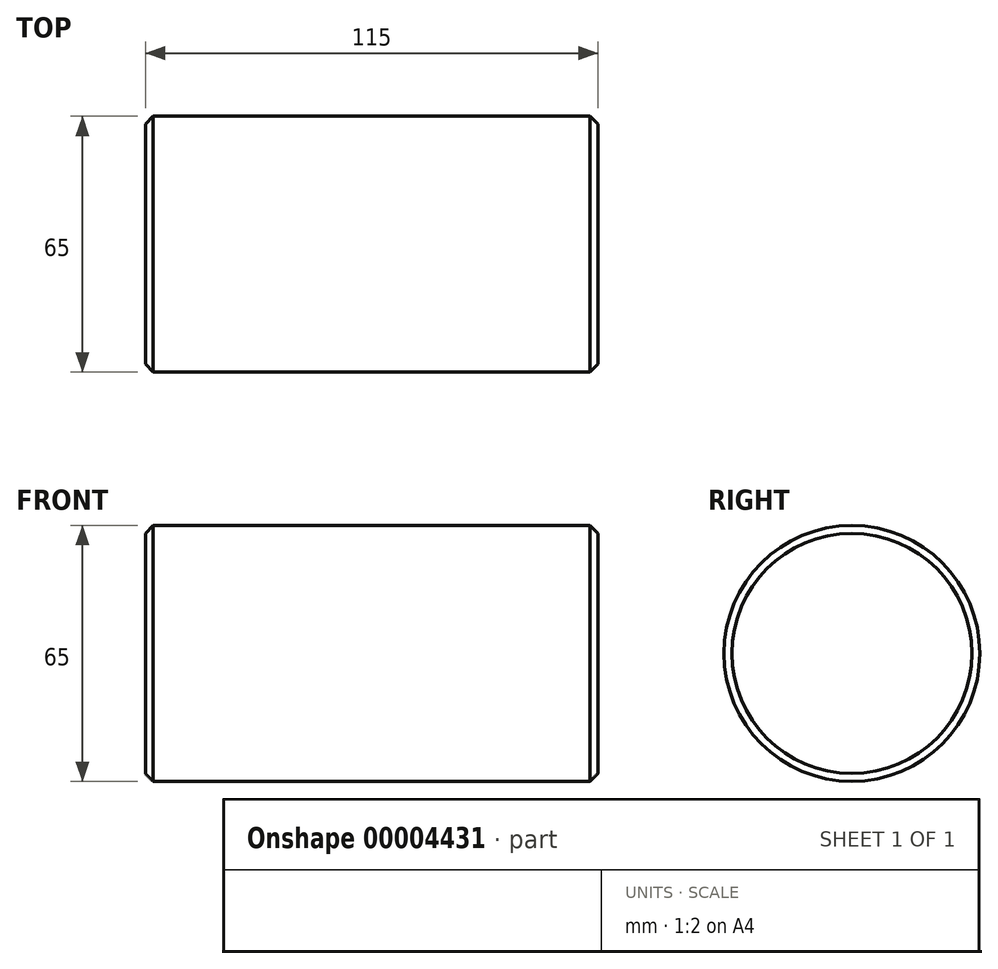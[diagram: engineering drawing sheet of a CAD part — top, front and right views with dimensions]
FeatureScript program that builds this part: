
annotation { "Feature Type Name" : "Feature", "Feature Type Description" : "" }
export const myFeature = defineFeature(function(context is Context, id is Id, definition is map)
    precondition{}
    {
        {
            var Q0;
            Q0=qCreatedBy(makeId("Right.planeOp"),FACE);
            var sketch = newSketch(context, id + "F0", { "sketchPlane" : qUnion([Q0])});
            skCircle(sketch, "E0", {"center": v(0, 0) * mm, "radius": 32.5 * mm});
            skSolve(sketch);
        }
        {
            var Q0;
            Q0 = qSketchRegion(id + "F0", true);
            extrude(context, id + "F1", {"entities" : qUnion([Q0]), "endBound" : BoundingType.SYMMETRIC, "depth" : 115 * mm});
        }
        {
            var Q0;
            Q0=makeQuery(id+"F1.opExtrude","CAP_EDGE",EDGE,{"disambiguationData":[OSD([sQuery(id+"F0.wireOp",EDGE,"E0")])],"isStart":true});
            var Q1;
            Q1=makeQuery(id+"F1.opExtrude","CAP_EDGE",EDGE,{"disambiguationData":[OSD([sQuery(id+"F0.wireOp",EDGE,"E0")])],"isStart":false});
            chamfer(context, id + "F2", {"entities" : qUnion([Q0, Q1]), "width" : 2 * mm, "tangentPropagation" : true});
        }
    });
